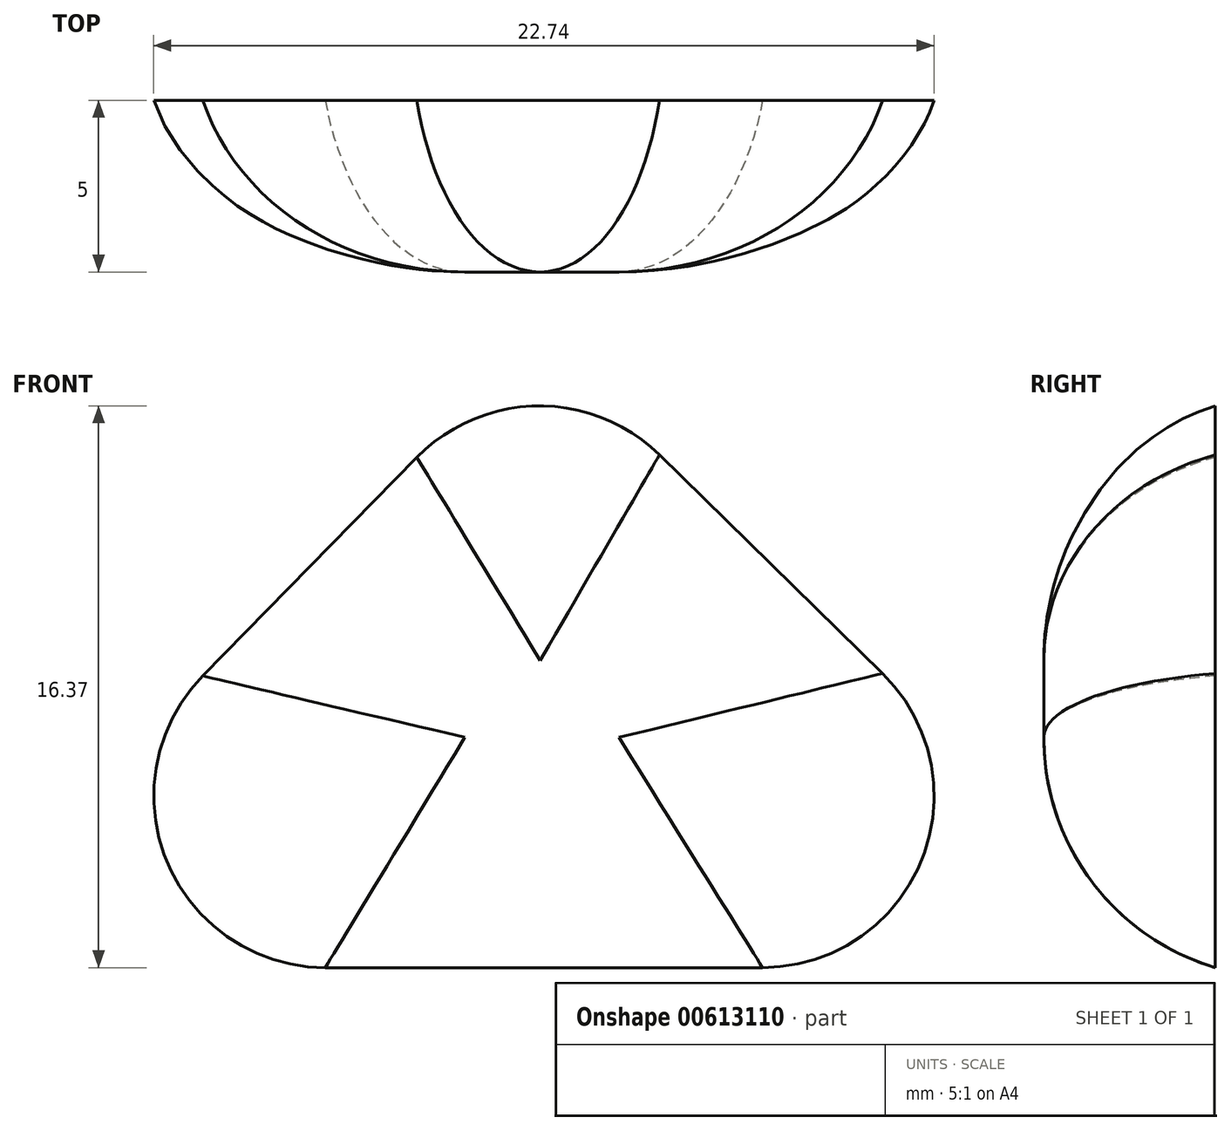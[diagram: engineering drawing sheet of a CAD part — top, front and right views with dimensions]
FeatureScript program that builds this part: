
annotation { "Feature Type Name" : "Feature", "Feature Type Description" : "" }
export const myFeature = defineFeature(function(context is Context, id is Id, definition is map)
    precondition{}
    {
        {
            var Q0;
            Q0=qCreatedBy(makeId("Front.planeOp"),FACE);
            var sketch = newSketch(context, id + "F0", { "sketchPlane" : qUnion([Q0])});
            skLineSegment(sketch, "E0", {"start": v(18.82, 0) * mm, "end": v(0, 18.44) * mm});
            skLineSegment(sketch, "E1", {"start": v(0, 18.44) * mm, "end": v(-18.06, 0) * mm});
            skLineSegment(sketch, "E2", {"start": v(-18.06, 0) * mm, "end": v(18.82, 0) * mm});
            skSolve(sketch);
        }
        {
            var Q0;
            Q0=makeQuery(id+"F0.imprint","IMPRINT",FACE,{"disambiguationData":[TD([[makeQuery(id+"F0.imprint","IMPRINT",EDGE,{"derivedFrom":sQuery(id+"F0.wireOp",EDGE,"E0")}),1.0]])]});
            extrude(context, id + "F1", {"entities" : qUnion([Q0]), "depth" : 5 * mm, "offsetDistance" : 25 * mm});
        }
        {
            var Q0;
            Q0=makeQuery(id+"F1.opExtrude","SWEPT_EDGE",EDGE,{"disambiguationData":[OSD([sQuery(id+"F0.wireOp",EDGE,"E0"),sQuery(id+"F0.wireOp",EDGE,"E1")])]});
            var Q1;
            Q1=makeQuery(id+"F1.opExtrude","SWEPT_EDGE",EDGE,{"disambiguationData":[OSD([sQuery(id+"F0.wireOp",EDGE,"E1"),sQuery(id+"F0.wireOp",EDGE,"E2")])]});
            var Q2;
            Q2=makeQuery(id+"F1.opExtrude","SWEPT_EDGE",EDGE,{"disambiguationData":[OSD([sQuery(id+"F0.wireOp",EDGE,"E0"),sQuery(id+"F0.wireOp",EDGE,"E2")])]});
            fillet(context, id + "F2", {"entities" : qUnion([Q0, Q1, Q2]), "radius" : 5 * mm, "tangentPropagation" : true, "allowEdgeOverflow" : false});
        }
        {
            var Q0;
            Q0=makeQuery(id+"F1.opExtrude","CAP_EDGE",EDGE,{"disambiguationData":[OSD([sQuery(id+"F0.wireOp",EDGE,"E1")])],"isStart":false});
            fillet(context, id + "F3", {"entities" : qUnion([Q0]), "radius" : 7 * mm, "tangentPropagation" : true, "allowEdgeOverflow" : false});
        }
    });
